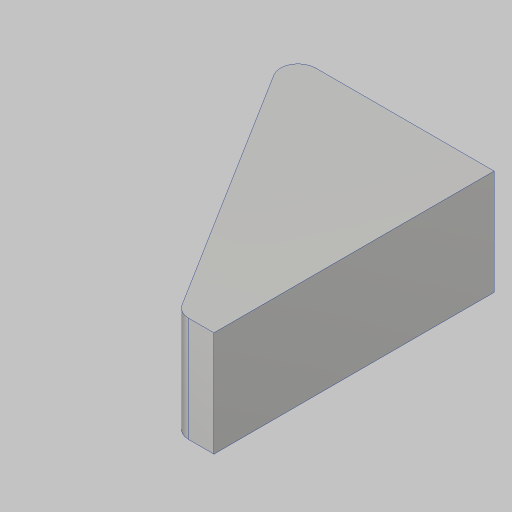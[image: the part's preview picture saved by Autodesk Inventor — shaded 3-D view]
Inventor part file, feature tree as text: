
AUTODESK INVENTOR PART (.ipt)
format: ipt  version: 2023.5 (Build 275446000, 446)  size: 89,600 bytes
history: native  units: in
note: dims shown in document units (in); Inventor stores cm internally (conversion verified against a paired STEP export)
features: extrude x1, fillet x1, sketch x1
ambient origin geometry x8: Origin, YZ Plane, XZ Plane, XY Plane, X Axis, Y Axis, Z Axis, Center Point
bodies: Solid1 (feature_tree)
feature tree (3):
  extrude  "Extrusion1"  Depth=0.25in
  fillet  "Fillet1"  Radius=4.0in
  sketch  "Sketch1"  dims[d0=0.5in d1=3.0in d2=4.0in d3=1.5in d4=0.0in d5=0.25in]
